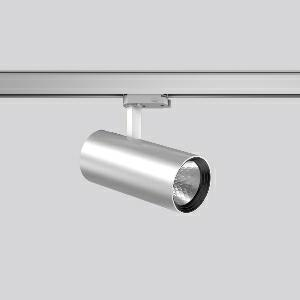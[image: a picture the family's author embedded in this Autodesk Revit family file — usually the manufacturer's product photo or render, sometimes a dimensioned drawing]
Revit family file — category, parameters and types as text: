
# Revit family: deecos_s_mini_742196_004_76_bbfb
name_source: partatom
category: Lighting Fixtures
units: mm (PartAtom-declared; Revit-internal decimal feet)

## family parameters
Cut with Voids When Loaded = No
Host = Face
Light Source = No
Part Type = Normal
Room Calculation Point = No
Round Connector Dimension = Use Diameter
Shared = No

## types (1)
- DEECOS S mini (1 x LED Modul 930, 2450 lm, 3000)
    Apparent Load = 20 VA
    Approval mark = CE
    CIE Flux Codes = 99 100 100 100 100
    Color Rendering = 90
    Color Temperature = 3000
    Default Elevation = 1800 mm
    Description = Series: DEECOS S mini
LED surface-mounted projector in modern design with no visible cooling ribs. Housing: die-cast aluminium, powder-coated. Rotation range: 356°. Swivel range: 90°. Black plastic ring and recessed LED to prevent glare from the side. Optical assembly with reflector made of MIRO-Silver with 98% total light reflection for outstanding efficiency - can be changed without tools. Best colour rendering index Ra>90. With adapter for RZB 3-circuit DALI tracks. Suitable for Track on ceiling, Wall track. High quality converter without flickering and stroboscopic effect. The following accessories can be mounted without use of tools: interchangeable lenses, decorative glasses, honeycomb louvre, clear and frosted diffusers, white interchangeable plastic ring. 
Colour: silver
Diameter: 87 mm
Height: 214 mm
Lamp: LED
Socket: without socket
Colour temperature: 3000K
Colour rendering index (CRI): 92
System power: 20 W
Rated luminous flux: 2450 lm
Luminous efficiency: 123 lm/W
Control gear: Converter, dimmable, DALI
Protection class: I
Type of protection: IP 20
    Height = 214 mm
    Lamp = 1 x LED Modul 930
    Lamp Light Flux = 2450 lm
    Lamp count = 1
    Length = 87 mm
    Lifetime = 50000 h
    Luminous efficacy = 123 lm/W
    Manufacturer = RZB
    ModVariant = No
    Model = 742196.004.76
    Mounting Place = Ceiling
    Mounting Type = Rail mounted
    Number of Poles = 1
    OnlyDefault = Yes
    Power Factor = 1
    Product Name = DEECOS S mini
    Product group = Track mounted projectors
    ProductGroupID = 301
    Protection Class = Protection class I
    Protection Degree = IP 20
    RLX_Detail_Level = 1
    RLX_Emergency_Light_Flux = 0 lm
    RLX_Emergency_Type = 0
    RLX_Emergency_Type_DB = No
    RlxData = <blob elided: 37381 chars, md5=e2b7e083>
    Socket = socket
    Standby Power = 0 W
    System Light Flux = 2450 lm
    System Power = 20 W
    Type Comments = Product without accessories
    Type Image = 741926.004.jpg
    URL = http://relux.com
    VarID = ---
    Voltage = 230 V
    Voltage Range = 220-240 V
    Weight = 0.00 kg
    Width = 0 mm  [stored 0 ft]

note: [stored X ft] marks values corroborated as IEEE doubles in the binary element streams (Revit-internal decimal feet)

## geometry (parser evidence)
native form markers: Blend x4, Sweep x12
no freeform markers — native parametric forms only
